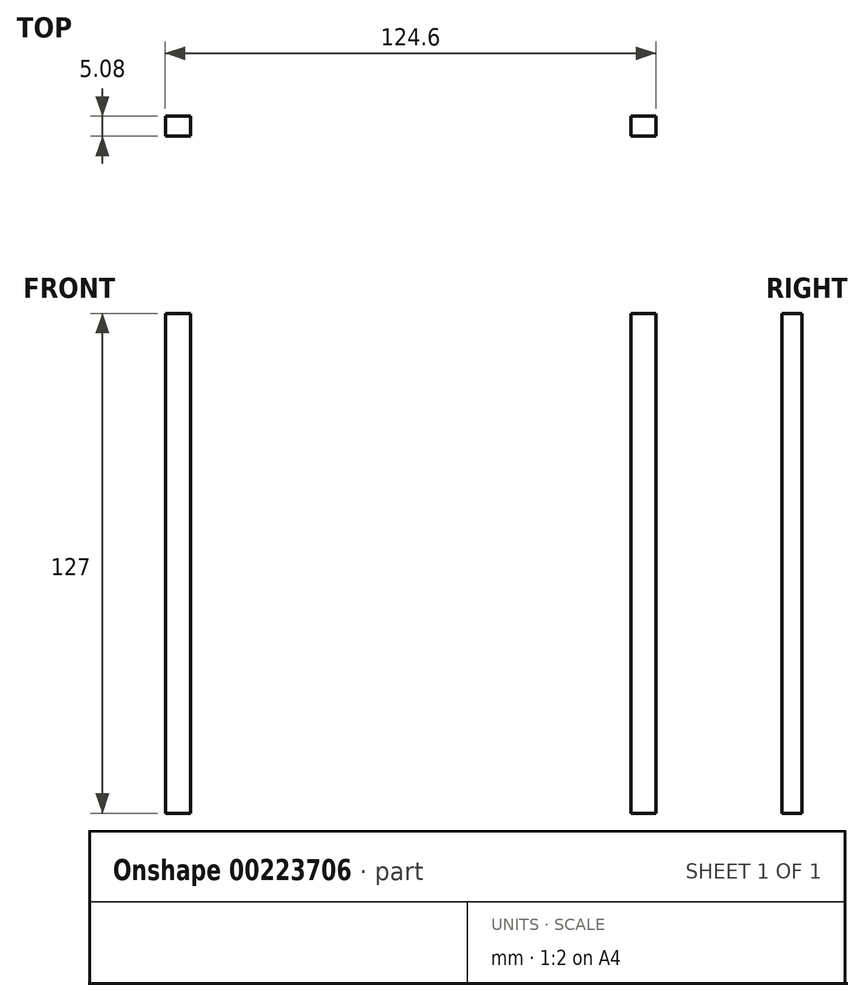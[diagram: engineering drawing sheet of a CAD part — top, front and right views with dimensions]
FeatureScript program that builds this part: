
annotation { "Feature Type Name" : "Feature", "Feature Type Description" : "" }
export const myFeature = defineFeature(function(context is Context, id is Id, definition is map)
    precondition{}
    {
        {
            var Q0;
            Q0=qCreatedBy(makeId("Front.planeOp"),FACE);
            var sketch = newSketch(context, id + "F0", { "sketchPlane" : qUnion([Q0])});
            skLineSegment(sketch, "E0.bottom", {"start": v(-62.3, 61.38) * mm, "end": v(-55.95, 61.38) * mm});
            skLineSegment(sketch, "E0.top", {"start": v(-62.3, -65.62) * mm, "end": v(-55.95, -65.62) * mm});
            skLineSegment(sketch, "E0.left", {"start": v(-62.3, 61.38) * mm, "end": v(-62.3, -65.62) * mm});
            skLineSegment(sketch, "E0.right", {"start": v(-55.95, 61.38) * mm, "end": v(-55.95, -65.62) * mm});
            skLineSegment(sketch, "E1.MirrorCS", {"start": v(55.95, 61.38) * mm, "end": v(55.95, -65.62) * mm});
            skLineSegment(sketch, "E2.MirrorCS", {"start": v(62.3, 61.38) * mm, "end": v(62.3, -65.62) * mm});
            skLineSegment(sketch, "E3.MirrorCS", {"start": v(62.3, 61.38) * mm, "end": v(55.95, 61.38) * mm});
            skLineSegment(sketch, "E4.MirrorCS", {"start": v(62.3, -65.62) * mm, "end": v(55.95, -65.62) * mm});
            skSolve(sketch);
        }
        {
            var Q0;
            Q0 = qSketchRegion(id + "F0", true);
            extrude(context, id + "F1", {"entities" : qUnion([Q0]), "endBound" : BoundingType.SYMMETRIC, "depth" : 5.08 * mm});
        }
    });
